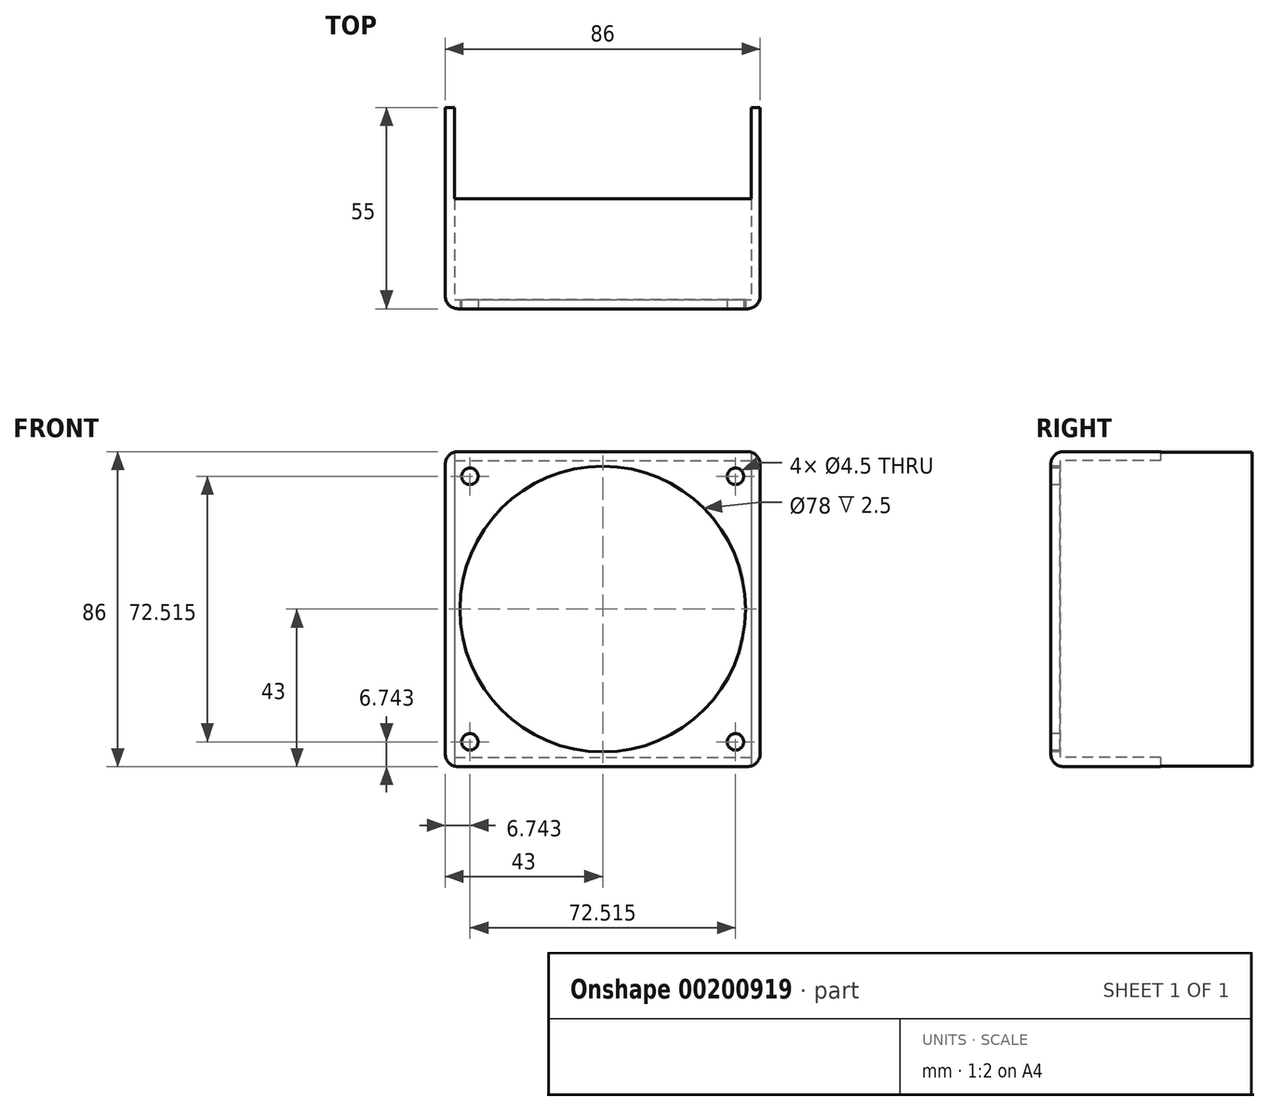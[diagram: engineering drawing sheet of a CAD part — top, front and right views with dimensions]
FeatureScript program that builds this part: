
annotation { "Feature Type Name" : "Feature", "Feature Type Description" : "" }
export const myFeature = defineFeature(function(context is Context, id is Id, definition is map)
    precondition{}
    {
        {
            var Q0;
            Q0=qCreatedBy(makeId("Front.planeOp"),FACE);
            var sketch = newSketch(context, id + "F0", { "sketchPlane" : qUnion([Q0])});
            skCircle(sketch, "E0", {"center": v(0, 0) * mm, "radius": 39 * mm});
            skLineSegment(sketch, "E1.bottom", {"start": v(-40.5, 40.5) * mm, "end": v(40.5, 40.5) * mm});
            skLineSegment(sketch, "E1.top", {"start": v(-40.5, -40.5) * mm, "end": v(40.5, -40.5) * mm});
            skLineSegment(sketch, "E1.left", {"start": v(-40.5, 40.5) * mm, "end": v(-40.5, -40.5) * mm});
            skLineSegment(sketch, "E1.right", {"start": v(40.5, 40.5) * mm, "end": v(40.5, -40.5) * mm});
            skCircle(sketch, "E2", {"center": v(-36.26, -36.26) * mm, "radius": 2.25 * mm});
            skCircle(sketch, "E3", {"center": v(-36.26, 36.26) * mm, "radius": 2.25 * mm});
            skCircle(sketch, "E4", {"center": v(36.26, 36.26) * mm, "radius": 2.25 * mm});
            skCircle(sketch, "E5", {"center": v(36.26, -36.26) * mm, "radius": 2.25 * mm});
            skLineSegment(sketch, "E6.bottom", {"start": v(40.5, -40.5) * mm, "end": v(40.5, -40.5) * mm});
            skLineSegment(sketch, "E6.top", {"start": v(40.5, 40.5) * mm, "end": v(40.5, 40.5) * mm});
            skLineSegment(sketch, "E6.left", {"start": v(40.5, -40.5) * mm, "end": v(40.5, 40.5) * mm});
            skLineSegment(sketch, "E6.right", {"start": v(40.5, -40.5) * mm, "end": v(40.5, 40.5) * mm});
            skLineSegment(sketch, "E7.bottom", {"start": v(43, 43) * mm, "end": v(-43, 43) * mm});
            skLineSegment(sketch, "E7.top", {"start": v(43, -43) * mm, "end": v(-43, -43) * mm});
            skLineSegment(sketch, "E7.left", {"start": v(43, 43) * mm, "end": v(43, -43) * mm});
            skLineSegment(sketch, "E7.right", {"start": v(-43, 43) * mm, "end": v(-43, -43) * mm});
            skSolve(sketch);
        }
        {
            var Q0;
            Q0=makeQuery(id+"F0.imprint","IMPRINT",FACE,{"disambiguationData":[TD([[makeQuery(id+"F0.imprint","IMPRINT",EDGE,{"derivedFrom":sQuery(id+"F0.wireOp",EDGE,"E0")}),-1.0]])]});
            extrude(context, id + "F1", {"entities" : qUnion([Q0]), "oppositeDirection" : true, "depth" : 2.5 * mm});
        }
        {
            var Q0;
            Q0=makeQuery(id+"F0.imprint","IMPRINT",FACE,{"disambiguationData":[TD([[makeQuery(id+"F0.imprint","IMPRINT",EDGE,{"derivedFrom":sQuery(id+"F0.wireOp",EDGE,"E1.bottom")}),1.0]])]});
            extrude(context, id + "F2", {"entities" : qUnion([Q0]), "operationType" : NewBodyOperationType.ADD, "oppositeDirection" : true, "depth" : 55 * mm});
        }
        {
            var Q0;
            Q0=makeQuery(id+"F2.opExtrude","SWEPT_FACE",FACE,{"disambiguationData":[OSD([sQuery(id+"F0.wireOp",EDGE,"E7.top")])]});
            var sketch = newSketch(context, id + "F3", { "sketchPlane" : qUnion([Q0])});
            skLineSegment(sketch, "E8.bottom", {"start": v(-40.5, -55) * mm, "end": v(40.5, -55) * mm});
            skLineSegment(sketch, "E8.top", {"start": v(-40.5, -30) * mm, "end": v(40.5, -30) * mm});
            skLineSegment(sketch, "E8.left", {"start": v(-40.5, -55) * mm, "end": v(-40.5, -30) * mm});
            skLineSegment(sketch, "E8.right", {"start": v(40.5, -55) * mm, "end": v(40.5, -30) * mm});
            skSolve(sketch);
        }
        {
            var Q0;
            Q0=makeQuery(id+"F3.imprint","IMPRINT",FACE,{"disambiguationData":[TD([[makeQuery(id+"F3.imprint","IMPRINT",EDGE,{"derivedFrom":sQuery(id+"F3.wireOp",EDGE,"E8.bottom")}),-1.0]])]});
            extrude(context, id + "F4", {"entities" : qUnion([Q0]), "operationType" : NewBodyOperationType.REMOVE, "oppositeDirection" : true, "depth" : 100 * mm});
        }
        {
            var Q0;
            Q0=makeQuery(id+"F2.opExtrude","CAP_EDGE",EDGE,{"disambiguationData":[OSD([sQuery(id+"F0.wireOp",EDGE,"E7.top")])],"isStart":true});
            var Q1;
            Q1=makeQuery(id+"F2.opExtrude","CAP_EDGE",EDGE,{"disambiguationData":[OSD([sQuery(id+"F0.wireOp",EDGE,"E7.right")])],"isStart":true});
            var Q2;
            Q2=makeQuery(id+"F2.opExtrude","CAP_EDGE",EDGE,{"disambiguationData":[OSD([sQuery(id+"F0.wireOp",EDGE,"E7.left")])],"isStart":true});
            var Q3;
            Q3=makeQuery(id+"F2.opExtrude","CAP_EDGE",EDGE,{"disambiguationData":[OSD([sQuery(id+"F0.wireOp",EDGE,"E7.bottom")])],"isStart":true});
            var Q4;
            Q4=makeQuery(id+"F2.opExtrude","SWEPT_EDGE",EDGE,{"disambiguationData":[OSD([sQuery(id+"F0.wireOp",EDGE,"E7.bottom"),sQuery(id+"F0.wireOp",EDGE,"E7.right")])]});
            var Q5;
            Q5=makeQuery(id+"F2.opExtrude","SWEPT_EDGE",EDGE,{"disambiguationData":[OSD([sQuery(id+"F0.wireOp",EDGE,"E7.top"),sQuery(id+"F0.wireOp",EDGE,"E7.right")])]});
            var Q6;
            Q6=makeQuery(id+"F2.opExtrude","SWEPT_EDGE",EDGE,{"disambiguationData":[OSD([sQuery(id+"F0.wireOp",EDGE,"E7.top"),sQuery(id+"F0.wireOp",EDGE,"E7.left")])]});
            var Q7;
            Q7=makeQuery(id+"F2.opExtrude","SWEPT_EDGE",EDGE,{"disambiguationData":[OSD([sQuery(id+"F0.wireOp",EDGE,"E7.bottom"),sQuery(id+"F0.wireOp",EDGE,"E7.left")])]});
            fillet(context, id + "F5", {"entities" : qUnion([Q0, Q1, Q2, Q3, Q4, Q5, Q6, Q7]), "radius" : 3.5 * mm, "tangentPropagation" : true, "allowEdgeOverflow" : false});
        }
    });
